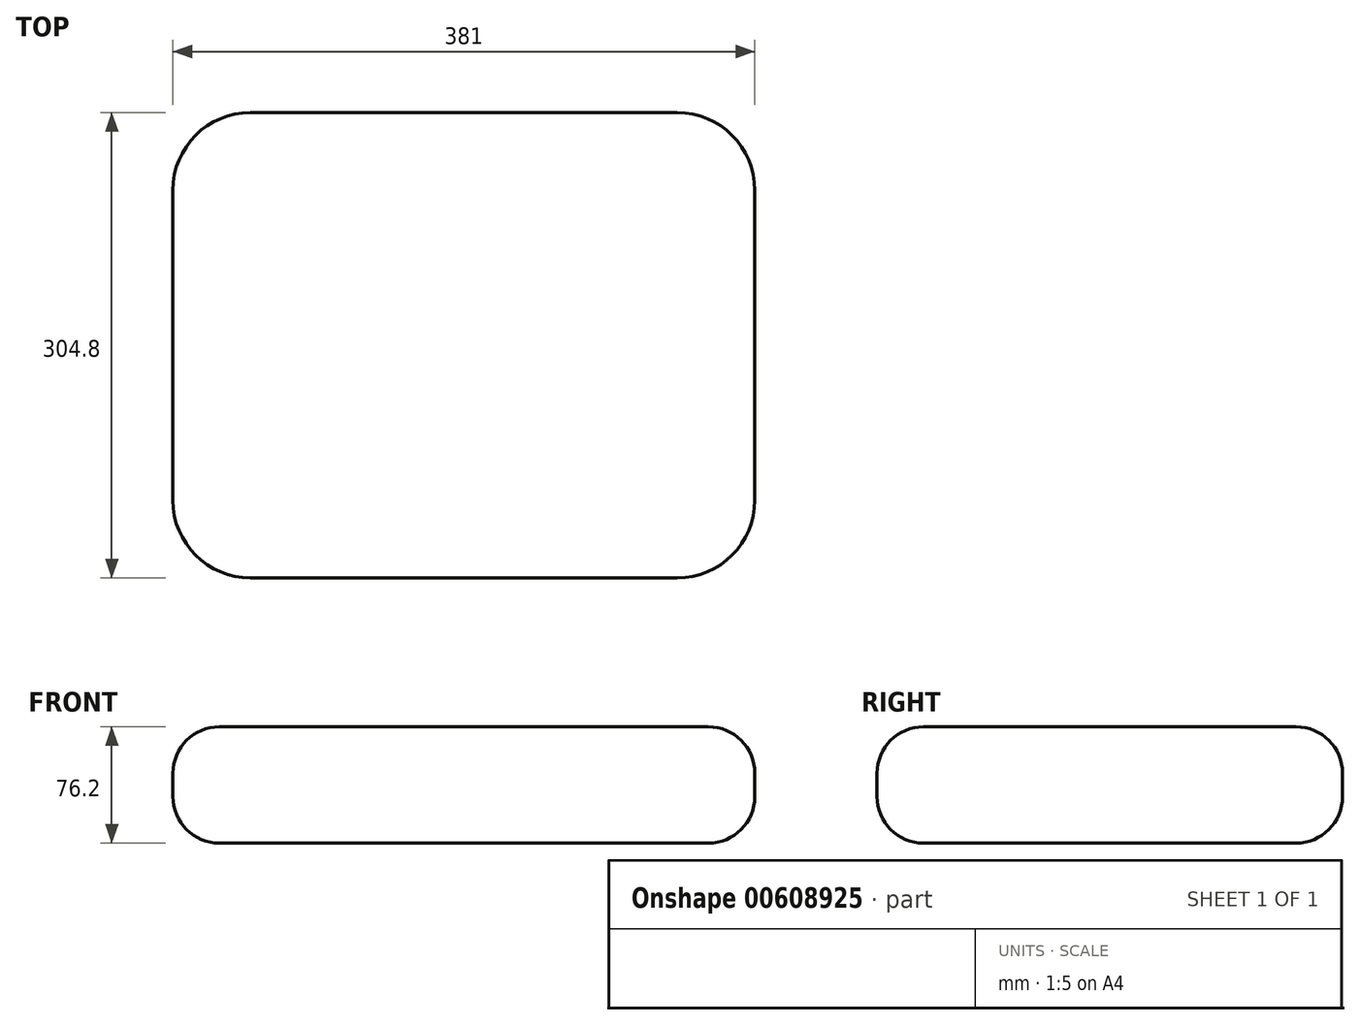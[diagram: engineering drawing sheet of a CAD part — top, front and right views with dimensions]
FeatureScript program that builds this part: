
annotation { "Feature Type Name" : "Feature", "Feature Type Description" : "" }
export const myFeature = defineFeature(function(context is Context, id is Id, definition is map)
    precondition{}
    {
        {
            var Q0;
            Q0=qCreatedBy(makeId("Top.planeOp"),FACE);
            var sketch = newSketch(context, id + "F0", { "sketchPlane" : qUnion([Q0])});
            skLineSegment(sketch, "E0.bottom", {"start": v(139.7, -152.4) * mm, "end": v(-139.7, -152.4) * mm});
            skLineSegment(sketch, "E0.top", {"start": v(139.7, 152.4) * mm, "end": v(-139.7, 152.4) * mm});
            skLineSegment(sketch, "E0.left", {"start": v(190.5, -101.6) * mm, "end": v(190.5, 101.6) * mm});
            skLineSegment(sketch, "E0.right", {"start": v(-190.5, -101.6) * mm, "end": v(-190.5, 101.6) * mm});
            skPoint(sketch, "E0.middle", {"position": v(0, 0) * mm});
            skPoint(sketch, "E1.visualSharp", {"position": v(-190.5, 152.4) * mm});
            skArc(sketch, "E1.filletArc", {"start": v(-139.7, 152.4) * mm, "mid": v(-175.62, 137.52) * mm, "end": v(-190.5, 101.6) * mm});
            skPoint(sketch, "E2.visualSharp", {"position": v(190.5, 152.4) * mm});
            skArc(sketch, "E2.filletArc", {"start": v(190.5, 101.6) * mm, "mid": v(175.62, 137.52) * mm, "end": v(139.7, 152.4) * mm});
            skPoint(sketch, "E3.visualSharp", {"position": v(190.5, -152.4) * mm});
            skArc(sketch, "E3.filletArc", {"start": v(139.7, -152.4) * mm, "mid": v(175.62, -137.52) * mm, "end": v(190.5, -101.6) * mm});
            skPoint(sketch, "E4.visualSharp", {"position": v(-190.5, -152.4) * mm});
            skArc(sketch, "E4.filletArc", {"start": v(-190.5, -101.6) * mm, "mid": v(-175.62, -137.52) * mm, "end": v(-139.7, -152.4) * mm});
            skSolve(sketch);
        }
        {
            var Q0;
            Q0=makeQuery(id+"F0.imprint","IMPRINT",FACE,{"disambiguationData":[TD([[makeQuery(id+"F0.imprint","IMPRINT",EDGE,{"derivedFrom":sQuery(id+"F0.wireOp",EDGE,"E0.bottom")}),-1.0]])]});
            extrude(context, id + "F1", {"entities" : qUnion([Q0]), "depth" : 38.1 * mm, "offsetDistance" : 25.4 * mm});
        }
        {
            var Q0;
            Q0=makeQuery(id+"F1.opExtrude","CAP_EDGE",EDGE,{"disambiguationData":[OSD([sQuery(id+"F0.wireOp",EDGE,"E0.bottom")])],"isStart":true});
            fillet(context, id + "F2", {"entities" : qUnion([Q0]), "radius" : 30.48 * mm, "tangentPropagation" : true, "allowEdgeOverflow" : false});
        }
        {
            var Q0;
            Q0=makeQuery(id+"F1.opExtrude","CAP_FACE",FACE,{"disambiguationData":[OSD([sQuery(id+"F0.wireOp",EDGE,"E0.bottom"),sQuery(id+"F0.wireOp",EDGE,"E0.top"),sQuery(id+"F0.wireOp",EDGE,"E0.left"),sQuery(id+"F0.wireOp",EDGE,"E0.right"),sQuery(id+"F0.wireOp",EDGE,"E1.filletArc"),sQuery(id+"F0.wireOp",EDGE,"E2.filletArc"),sQuery(id+"F0.wireOp",EDGE,"E3.filletArc"),sQuery(id+"F0.wireOp",EDGE,"E4.filletArc")])],"isStart":false});
            extrude(context, id + "F3", {"entities" : qUnion([Q0]), "operationType" : NewBodyOperationType.ADD, "depth" : 38.1 * mm, "offsetDistance" : 25.4 * mm});
        }
        {
            var Q0;
            Q0=makeQuery(id+"F3.opExtrude","CAP_EDGE",EDGE,{"disambiguationData":[OSD([sQuery(id+"F0.wireOp",EDGE,"E0.bottom")])],"isStart":false});
            fillet(context, id + "F4", {"entities" : qUnion([Q0]), "radius" : 30.48 * mm, "tangentPropagation" : true, "allowEdgeOverflow" : false});
        }
    });
